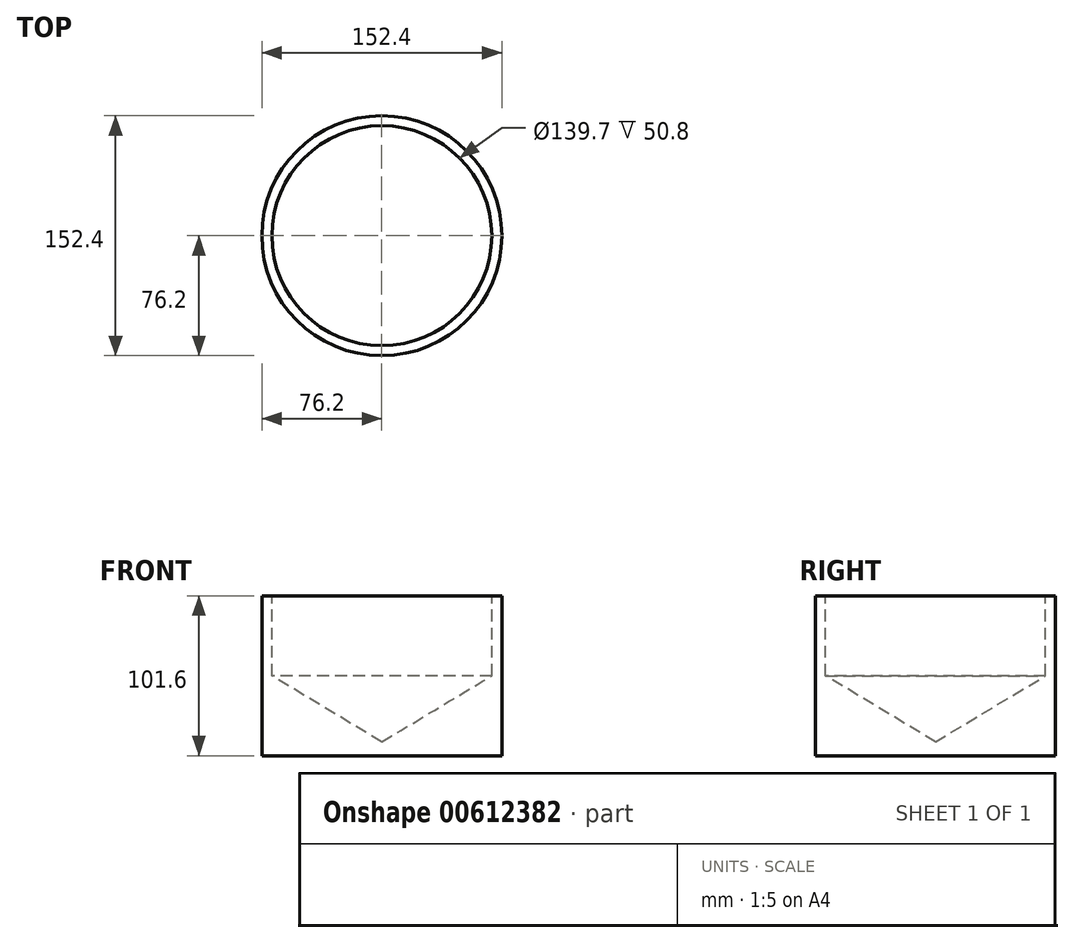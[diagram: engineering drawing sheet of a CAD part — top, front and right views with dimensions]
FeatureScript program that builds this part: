
annotation { "Feature Type Name" : "Feature", "Feature Type Description" : "" }
export const myFeature = defineFeature(function(context is Context, id is Id, definition is map)
    precondition{}
    {
        {
            var Q0;
            Q0=qCreatedBy(makeId("Top.planeOp"),FACE);
            var sketch = newSketch(context, id + "F0", { "sketchPlane" : qUnion([Q0])});
            skCircle(sketch, "E0", {"center": v(0, 0) * mm, "radius": 76.2 * mm});
            skSolve(sketch);
        }
        {
            var Q0;
            Q0 = qSketchRegion(id + "F0", true);
            extrude(context, id + "F1", {"entities" : qUnion([Q0]), "depth" : 101.6 * mm, "offsetDistance" : 25.4 * mm});
        }
        {
            var Q0;
            Q0=makeQuery(id+"F1.opExtrude","CAP_FACE",FACE,{"disambiguationData":[OSD([sQuery(id+"F0.wireOp",EDGE,"E0")])],"isStart":false});
            var sketch = newSketch(context, id + "F2", { "sketchPlane" : qUnion([Q0])});
            skCircle(sketch, "E1", {"center": v(0, 0) * mm, "radius": 46.38 * mm});
            skSolve(sketch);
        }
        {
            var Q0;
            Q0=sQuery(id+"F2.wireOp",VERTEX,"E1.center");
            var Q1;
            Q1=makeQuery(id+"F1.opExtrude","SWEPT_BODY",BODY,{"disambiguationData":[OSD([sQuery(id+"F0.wireOp",EDGE,"E0")])]});
            hole(context, id + "F3", {"style" : HoleStyle.SIMPLE, "endStyle" : HoleEndStyle.BLIND, "holeDiameter" : 139.7 * mm, "majorDiameter" : 6.35 * mm, "holeDepth" : 50.8 * mm, "isTappedThrough" : true, "tappedDepth" : 12.7 * mm, "tapClearance" : 3, "startFromSketch" : true, "locations" : qUnion([Q0]), "scope" : qUnion([Q1])});
        }
    });
